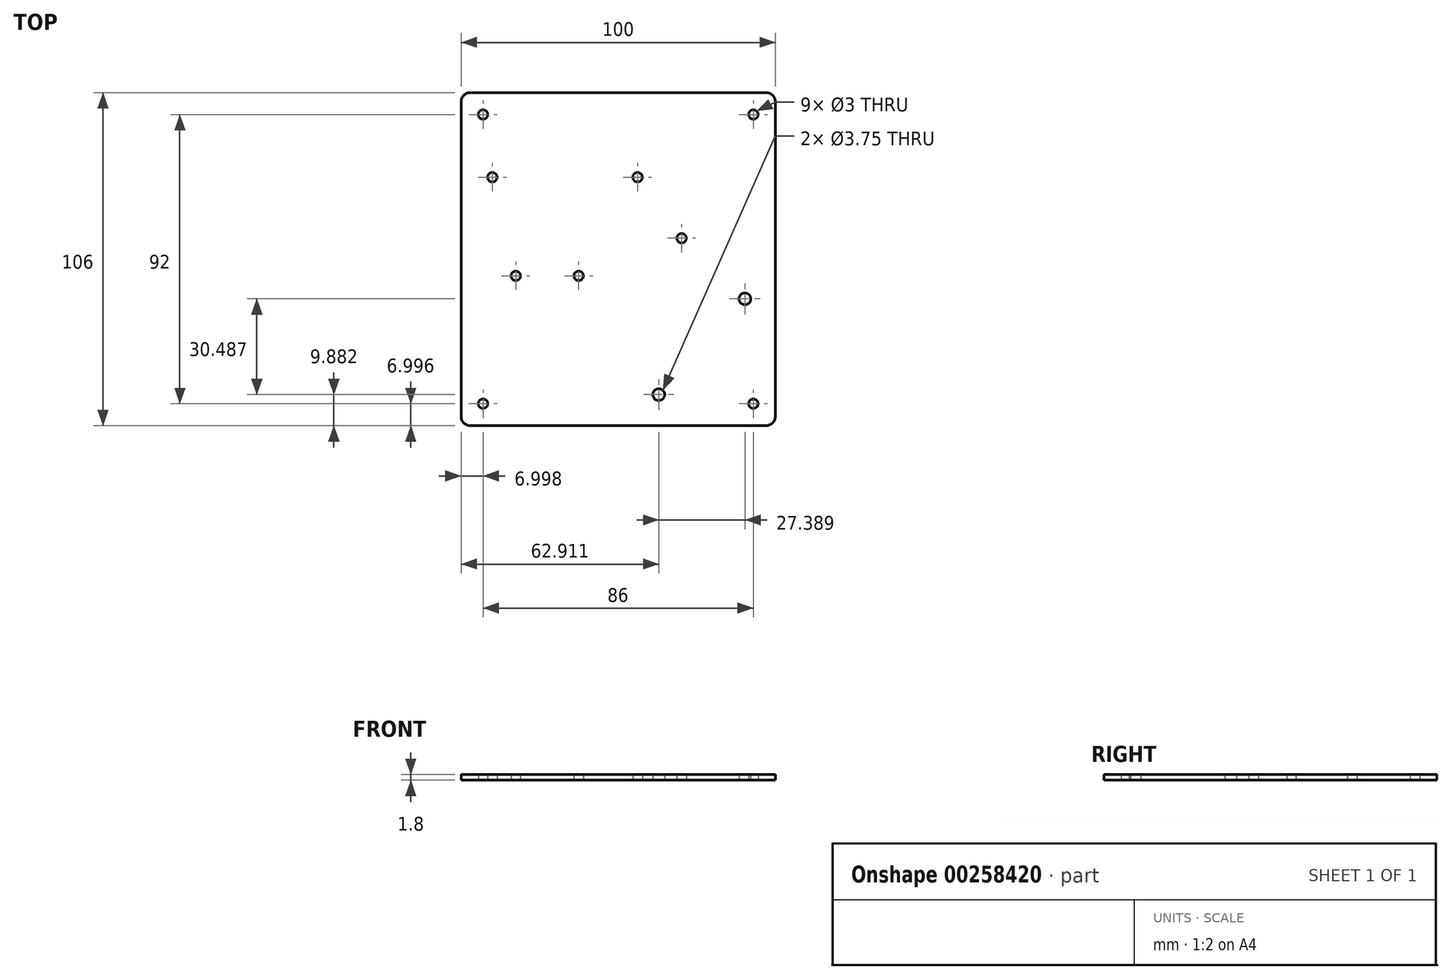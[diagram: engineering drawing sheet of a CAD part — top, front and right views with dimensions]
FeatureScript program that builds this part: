
annotation { "Feature Type Name" : "Feature", "Feature Type Description" : "" }
export const myFeature = defineFeature(function(context is Context, id is Id, definition is map)
    precondition{}
    {
        {
            var Q0;
            Q0=qCreatedBy(makeId("Top.planeOp"),FACE);
            var sketch = newSketch(context, id + "F0", { "sketchPlane" : qUnion([Q0])});
            skLineSegment(sketch, "E0.bottom", {"start": v(-4.34, -18.82) * mm, "end": v(-98.34, -18.82) * mm});
            skLineSegment(sketch, "E0.top", {"start": v(-4.34, 87.18) * mm, "end": v(-98.34, 87.18) * mm});
            skLineSegment(sketch, "E0.left", {"start": v(-1.34, -15.82) * mm, "end": v(-1.34, 84.18) * mm});
            skLineSegment(sketch, "E0.right", {"start": v(-101.34, -15.82) * mm, "end": v(-101.34, 84.18) * mm});
            skCircle(sketch, "E1", {"center": v(-91.39, 60.22) * mm, "radius": 1.5 * mm});
            skCircle(sketch, "E2", {"center": v(-45.17, 60.22) * mm, "radius": 1.5 * mm});
            skPoint(sketch, "E3.visualSharp", {"position": v(-101.34, 87.18) * mm});
            skArc(sketch, "E3.filletArc", {"start": v(-98.34, 87.18) * mm, "mid": v(-100.46, 86.3) * mm, "end": v(-101.34, 84.18) * mm});
            skPoint(sketch, "E4.visualSharp", {"position": v(-1.34, 87.18) * mm});
            skArc(sketch, "E4.filletArc", {"start": v(-1.34, 84.18) * mm, "mid": v(-2.22, 86.3) * mm, "end": v(-4.34, 87.18) * mm});
            skPoint(sketch, "E5.visualSharp", {"position": v(-1.34, -18.82) * mm});
            skArc(sketch, "E5.filletArc", {"start": v(-4.34, -18.82) * mm, "mid": v(-2.22, -17.95) * mm, "end": v(-1.34, -15.82) * mm});
            skPoint(sketch, "E6.visualSharp", {"position": v(-101.34, -18.82) * mm});
            skArc(sketch, "E6.filletArc", {"start": v(-101.34, -15.82) * mm, "mid": v(-100.46, -17.95) * mm, "end": v(-98.34, -18.82) * mm});
            skCircle(sketch, "E7.MirrorC", {"center": v(-8.34, 80.18) * mm, "radius": 1.5 * mm});
            skCircle(sketch, "E8", {"center": v(-11.04, 21.55) * mm, "radius": 1.88 * mm});
            skCircle(sketch, "E9", {"center": v(-38.43, -8.94) * mm, "radius": 1.88 * mm});
            skPoint(sketch, "E10.middle", {"position": v(-61.57, -13.8) * mm});
            skCircle(sketch, "E11", {"center": v(-31.18, 40.83) * mm, "radius": 1.5 * mm});
            skCircle(sketch, "E12.MirrorC", {"center": v(-100.32, 211.79) * mm, "radius": 1.5 * mm});
            skLineSegment(sketch, "E13", {"start": v(-51.34, 87.18) * mm, "end": v(-51.34, -18.82) * mm, "construction": true});
            skLineSegment(sketch, "E14", {"start": v(-101.34, 34.18) * mm, "end": v(-1.34, 34.18) * mm, "construction": true});
            skCircle(sketch, "E15", {"center": v(-63.92, 28.84) * mm, "radius": 1.5 * mm});
            skCircle(sketch, "E16", {"center": v(-83.92, 28.84) * mm, "radius": 1.5 * mm});
            skCircle(sketch, "E17.MirrorC", {"center": v(-94.34, 80.18) * mm, "radius": 1.5 * mm});
            skCircle(sketch, "E18.MirrorC", {"center": v(-8.34, -11.82) * mm, "radius": 1.5 * mm});
            skCircle(sketch, "E19.MirrorC", {"center": v(-94.34, -11.82) * mm, "radius": 1.5 * mm});
            skSolve(sketch);
        }
        {
            var Q0;
            Q0=makeQuery(id+"F0.imprint","IMPRINT",FACE,{"disambiguationData":[TD([[makeQuery(id+"F0.imprint","IMPRINT",EDGE,{"derivedFrom":sQuery(id+"F0.wireOp",EDGE,"E0.bottom")}),-1.0]])]});
            extrude(context, id + "F1", {"entities" : qUnion([Q0]), "depth" : 1.8 * mm});
        }
    });
